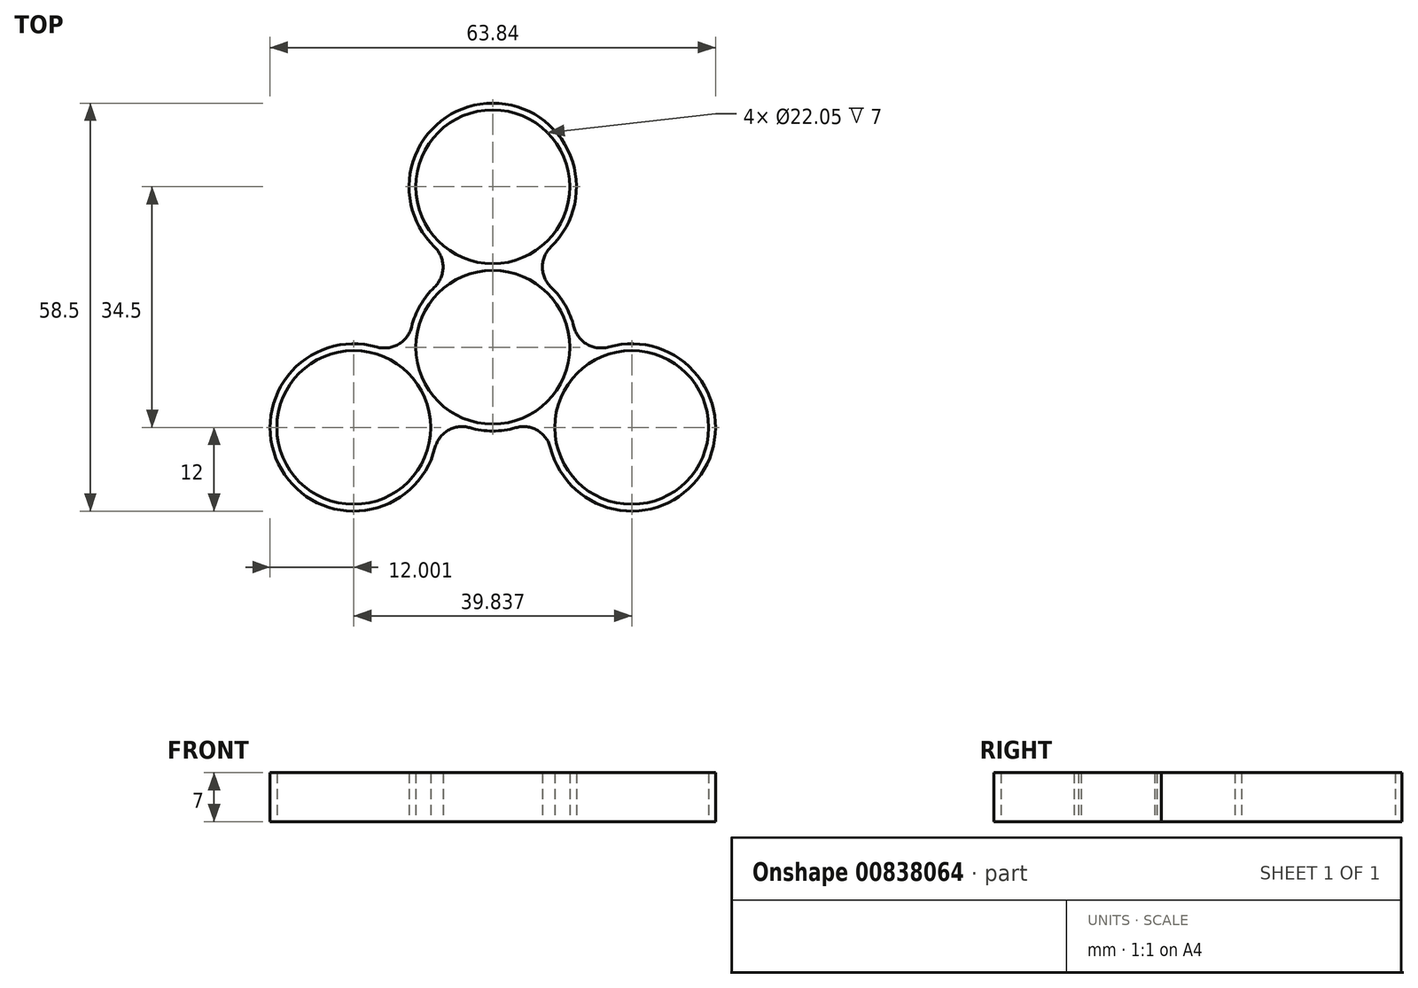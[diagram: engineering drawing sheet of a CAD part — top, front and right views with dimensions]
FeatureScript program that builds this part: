
annotation { "Feature Type Name" : "Feature", "Feature Type Description" : "" }
export const myFeature = defineFeature(function(context is Context, id is Id, definition is map)
    precondition{}
    {
        {
            var Q0;
            Q0=qCreatedBy(makeId("Top.planeOp"),FACE);
            var sketch = newSketch(context, id + "F0", { "sketchPlane" : qUnion([Q0])});
            skCircle(sketch, "E0", {"center": v(0, 0) * mm, "radius": 11.03 * mm});
            skCircle(sketch, "E1", {"center": v(0, 23) * mm, "radius": 11.03 * mm});
            skCircle(sketch, "E2.1.0", {"center": v(-19.92, -11.5) * mm, "radius": 11.03 * mm});
            skCircle(sketch, "E2.2.0", {"center": v(19.92, -11.5) * mm, "radius": 11.03 * mm});
            skArc(sketch, "E3", {"start": v(8.34, 14.38) * mm, "mid": v(0, 35) * mm, "end": v(-8.34, 14.38) * mm});
            skArc(sketch, "E4.1.0", {"start": v(-16.62, 0.04) * mm, "mid": v(-30.31, -17.5) * mm, "end": v(-8.28, -14.41) * mm});
            skArc(sketch, "E4.2.0", {"start": v(9.8, -5.04) * mm, "mid": v(9.53, -5.5) * mm, "end": v(9.27, -5.97) * mm});
            skArc(sketch, "E5", {"start": v(0.54, 11.99) * mm, "mid": v(0, 12) * mm, "end": v(-0.54, 11.99) * mm});
            skArc(sketch, "E6.trimOffspring", {"start": v(-8.34, 8.62) * mm, "mid": v(-10.4, 6) * mm, "end": v(-11.64, 2.91) * mm});
            skArc(sketch, "E7.trimOffspring", {"start": v(-0.54, 11.01) * mm, "mid": v(0, 11) * mm, "end": v(0.54, 11.01) * mm});
            skArc(sketch, "E8.trimOffspring", {"start": v(11.64, 2.91) * mm, "mid": v(10.4, 6) * mm, "end": v(8.34, 8.62) * mm});
            skArc(sketch, "E9.trimOffspring", {"start": v(10.11, -6.46) * mm, "mid": v(10.4, -6) * mm, "end": v(10.65, -5.53) * mm});
            skArc(sketch, "E10.trimOffspring", {"start": v(8.28, -14.41) * mm, "mid": v(30.31, -17.5) * mm, "end": v(16.62, 0.04) * mm});
            skArc(sketch, "E11.trimOffspring", {"start": v(-9.27, -5.97) * mm, "mid": v(-9.53, -5.5) * mm, "end": v(-9.8, -5.04) * mm});
            skArc(sketch, "E12.trimOffspring", {"start": v(-3.3, -11.54) * mm, "mid": v(0, -12) * mm, "end": v(3.3, -11.54) * mm});
            skArc(sketch, "E13.trimOffspring", {"start": v(-10.65, -5.53) * mm, "mid": v(-10.4, -6) * mm, "end": v(-10.11, -6.46) * mm});
            skPoint(sketch, "E14.visualSharp", {"position": v(-8.25, -8.72) * mm});
            skArc(sketch, "E14.filletArc", {"start": v(-3.3, -11.54) * mm, "mid": v(-6.4, -11.92) * mm, "end": v(-8.28, -14.41) * mm});
            skPoint(sketch, "E15.visualSharp", {"position": v(-11.67, -2.78) * mm});
            skArc(sketch, "E15.filletArc", {"start": v(-16.62, 0.04) * mm, "mid": v(-13.52, 0.42) * mm, "end": v(-11.64, 2.91) * mm});
            skPoint(sketch, "E16.visualSharp", {"position": v(-3.43, 11.5) * mm});
            skArc(sketch, "E16.filletArc", {"start": v(-8.34, 8.62) * mm, "mid": v(-7.12, 11.5) * mm, "end": v(-8.34, 14.37) * mm});
            skPoint(sketch, "E17.visualSharp", {"position": v(3.43, 11.5) * mm});
            skArc(sketch, "E17.filletArc", {"start": v(8.34, 14.37) * mm, "mid": v(7.12, 11.5) * mm, "end": v(8.34, 8.62) * mm});
            skPoint(sketch, "E18.visualSharp", {"position": v(11.67, -2.78) * mm});
            skArc(sketch, "E18.filletArc", {"start": v(11.64, 2.91) * mm, "mid": v(13.52, 0.42) * mm, "end": v(16.62, 0.04) * mm});
            skPoint(sketch, "E19.visualSharp", {"position": v(8.25, -8.72) * mm});
            skArc(sketch, "E19.filletArc", {"start": v(8.28, -14.41) * mm, "mid": v(6.4, -11.92) * mm, "end": v(3.3, -11.54) * mm});
            skCircle(sketch, "E20", {"center": v(-48.38, 40.77) * mm, "radius": 11 * mm});
            skSolve(sketch);
        }
        {
            var Q0;
            Q0=makeQuery(id+"F0.imprint","IMPRINT",FACE,{"disambiguationData":[TD([[makeQuery(id+"F0.imprint","IMPRINT",EDGE,{"derivedFrom":sQuery(id+"F0.wireOp",EDGE,"E3")}),1.0]])]});
            extrude(context, id + "F1", {"entities" : qUnion([Q0]), "depth" : 7 * mm, "offsetDistance" : 25 * mm});
        }
    });
